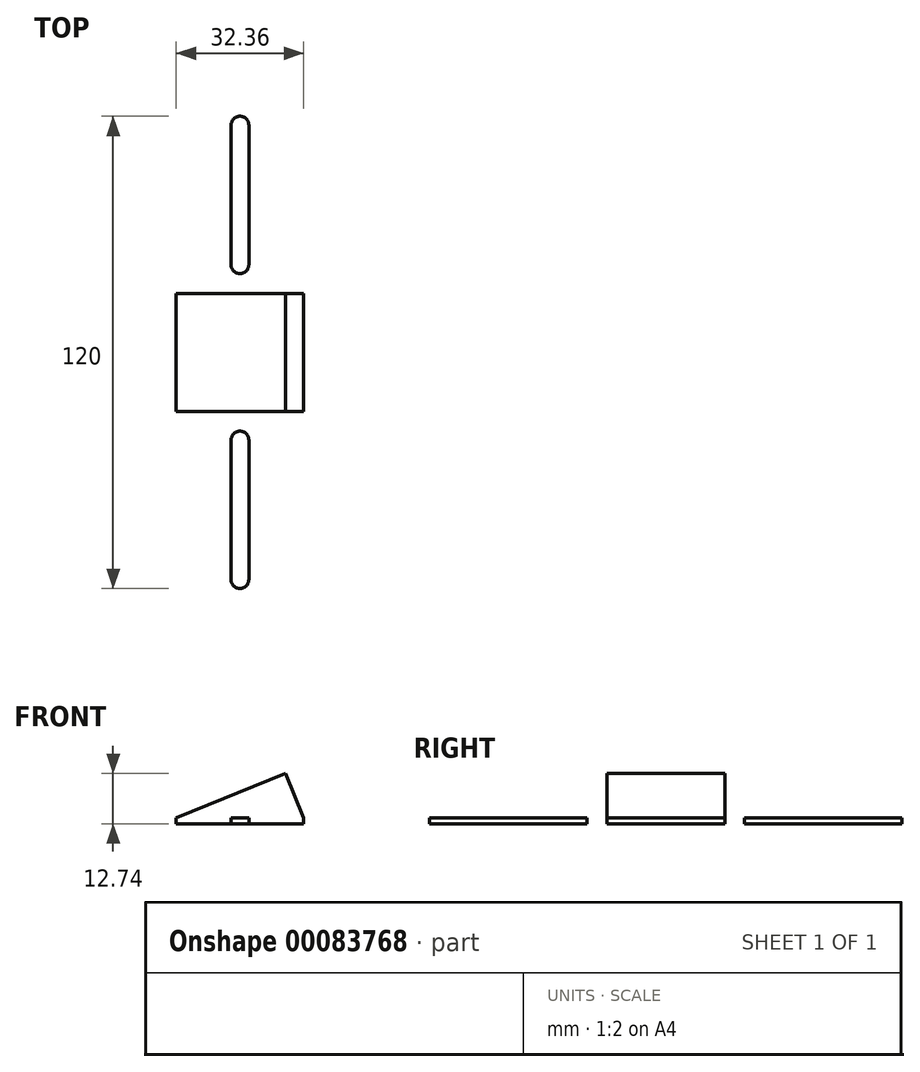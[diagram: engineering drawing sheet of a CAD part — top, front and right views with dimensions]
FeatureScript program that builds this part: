
annotation { "Feature Type Name" : "Feature", "Feature Type Description" : "" }
export const myFeature = defineFeature(function(context is Context, id is Id, definition is map)
    precondition{}
    {
        {
            var Q0;
            Q0=qCreatedBy(makeId("Front.planeOp"),FACE);
            var sketch = newSketch(context, id + "F0", { "sketchPlane" : qUnion([Q0])});
            skLineSegment(sketch, "E0", {"start": v(0, 1.5) * mm, "end": v(-32.36, 1.5) * mm});
            skLineSegment(sketch, "E1", {"start": v(0, 1.5) * mm, "end": v(0, 18.49) * mm, "construction": true});
            skLineSegment(sketch, "E2", {"start": v(0, 1.5) * mm, "end": v(-4.54, 12.74) * mm});
            skLineSegment(sketch, "E3", {"start": v(-4.54, 12.74) * mm, "end": v(-32.36, 1.5) * mm});
            skLineSegment(sketch, "E4", {"start": v(0, 0) * mm, "end": v(-32.36, 0) * mm});
            skLineSegment(sketch, "E5", {"start": v(-32.36, 0) * mm, "end": v(-32.36, 1.5) * mm});
            skLineSegment(sketch, "E6", {"start": v(0, 0) * mm, "end": v(0, 1.5) * mm});
            skSolve(sketch);
        }
        {
            var Q0;
            Q0 = qSketchRegion(id + "F0", true);
            extrude(context, id + "F1", {"entities" : qUnion([Q0]), "depth" : 15 * mm});
        }
        {
            var Q0;
            Q0=makeQuery(id+"F0.imprint","IMPRINT",FACE,{"disambiguationData":[TD([[makeQuery(id+"F0.imprint","IMPRINT",EDGE,{"derivedFrom":sQuery(id+"F0.wireOp",EDGE,"E0")}),1.0]])]});
            extrude(context, id + "F2", {"entities" : qUnion([Q0]), "operationType" : NewBodyOperationType.ADD, "oppositeDirection" : true, "depth" : 50 * mm});
        }
        {
            var Q0;
            Q0=makeQuery(id+"F2.opExtrude","CAP_EDGE",EDGE,{"disambiguationData":[OSD([sQuery(id+"F0.wireOp",EDGE,"E6")])],"isStart":false});
            var Q1;
            Q1=makeQuery(id+"F2.opExtrude","CAP_EDGE",EDGE,{"disambiguationData":[OSD([sQuery(id+"F0.wireOp",EDGE,"E5")])],"isStart":false});
            fillet(context, id + "F3", {"entities" : qUnion([Q0, Q1]), "radius" : 15 * mm, "tangentPropagation" : true, "allowEdgeOverflow" : false});
        }
        {
            var Q0;
            Q0=makeQuery(id+"F2.opExtrude","SWEPT_FACE",FACE,{"disambiguationData":[OSD([sQuery(id+"F0.wireOp",EDGE,"E0")])]});
            var sketch = newSketch(context, id + "F4", { "sketchPlane" : qUnion([Q0])});
            skLineSegment(sketch, "E7", {"start": v(-16.18, 0) * mm, "end": v(-16.18, 50) * mm, "construction": true});
            skLineSegment(sketch, "E8", {"start": v(-16.18, 42.75) * mm, "end": v(-16.18, 7.25) * mm});
            skArc(sketch, "E9.0.startCap", {"start": v(-18.43, 42.75) * mm, "mid": v(-16.18, 45) * mm, "end": v(-13.93, 42.75) * mm});
            skArc(sketch, "E9.0.endCap", {"start": v(-13.93, 7.25) * mm, "mid": v(-16.18, 5) * mm, "end": v(-18.43, 7.25) * mm});
            skLineSegment(sketch, "E9.0.left", {"start": v(-13.93, 42.75) * mm, "end": v(-13.93, 7.25) * mm});
            skLineSegment(sketch, "E9.0.right", {"start": v(-18.43, 42.75) * mm, "end": v(-18.43, 7.25) * mm});
            skSolve(sketch);
        }
        {
            var Q0;
            Q0=makeQuery(id+"F4.imprint","IMPRINT",FACE,{"disambiguationData":[TD([[makeQuery(id+"F4.imprint","IMPRINT",EDGE,{"derivedFrom":sQuery(id+"F4.wireOp",EDGE,"E9.0.startCap")}),-1.0]])]});
            var Q1;
            {var subQ0=sQuery(id+"F0.wireOp",EDGE,"E4");Q1=makeQuery(id+"F2.boolean.opBoolean","MERGE",FACE,{"derivedFrom":[makeQuery(id+"F1.opExtrude","SWEPT_FACE",FACE,{"disambiguationData":[OSD([subQ0])]}),makeQuery(id+"F2.opExtrude","SWEPT_FACE",FACE,{"disambiguationData":[OSD([subQ0])]})]});}
            extrude(context, id + "F5", {"entities" : qUnion([Q0]), "operationType" : NewBodyOperationType.REMOVE, "endBound" : BoundingType.UP_TO_SURFACE, "oppositeDirection" : true, "endBoundEntityFace" : qUnion([Q1]), "depth" : 25 * mm});
        }
        {
            var Q0;
            Q0=makeQuery(id+"F1.opExtrude","SWEPT_BODY",BODY,{"disambiguationData":[OSD([sQuery(id+"F0.wireOp",EDGE,"E2"),sQuery(id+"F0.wireOp",EDGE,"E3"),sQuery(id+"F0.wireOp",EDGE,"E4"),sQuery(id+"F0.wireOp",EDGE,"E5"),sQuery(id+"F0.wireOp",EDGE,"E6")])]});
            var Q1;
            Q1=makeQuery(id+"F1.opExtrude","CAP_FACE",FACE,{"disambiguationData":[OSD([sQuery(id+"F0.wireOp",EDGE,"E2"),sQuery(id+"F0.wireOp",EDGE,"E3"),sQuery(id+"F0.wireOp",EDGE,"E4"),sQuery(id+"F0.wireOp",EDGE,"E5"),sQuery(id+"F0.wireOp",EDGE,"E6")])],"isStart":false});
            mirror(context, id + "F6", {"operationType" : NewBodyOperationType.ADD, "entities" : qUnion([Q0]), "mirrorPlane" : qUnion([Q1])});
        }
    });
